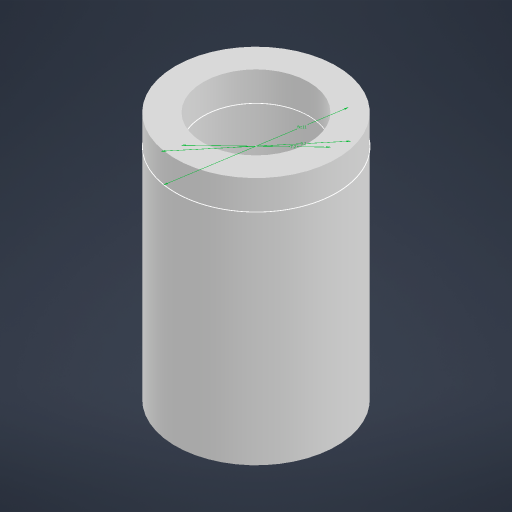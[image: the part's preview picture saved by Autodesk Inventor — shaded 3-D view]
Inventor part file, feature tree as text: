
AUTODESK INVENTOR PART (.ipt)
format: ipt  version: 2024.1 (Build 281209000, 209)  size: 160,256 bytes
history: native  units: mm
features: extrude x2, sketch x1
ambient origin geometry x8: Origin, YZ Plane, XZ Plane, XY Plane, X Axis, Y Axis, Z Axis, Center Point
bodies: Solid1 (feature_tree)
feature tree (3):
  sketch  "Sketch1"  dims[d0=11.0mm d1=7.2mm d2=9.2mm d3=2.0mm d4=0.0mm d5=15.0mm d6=0.0mm]
  extrude  "Extrusion1"  Depth=15.0mm
  extrude  "Extrusion2"  Depth=15.0mm
